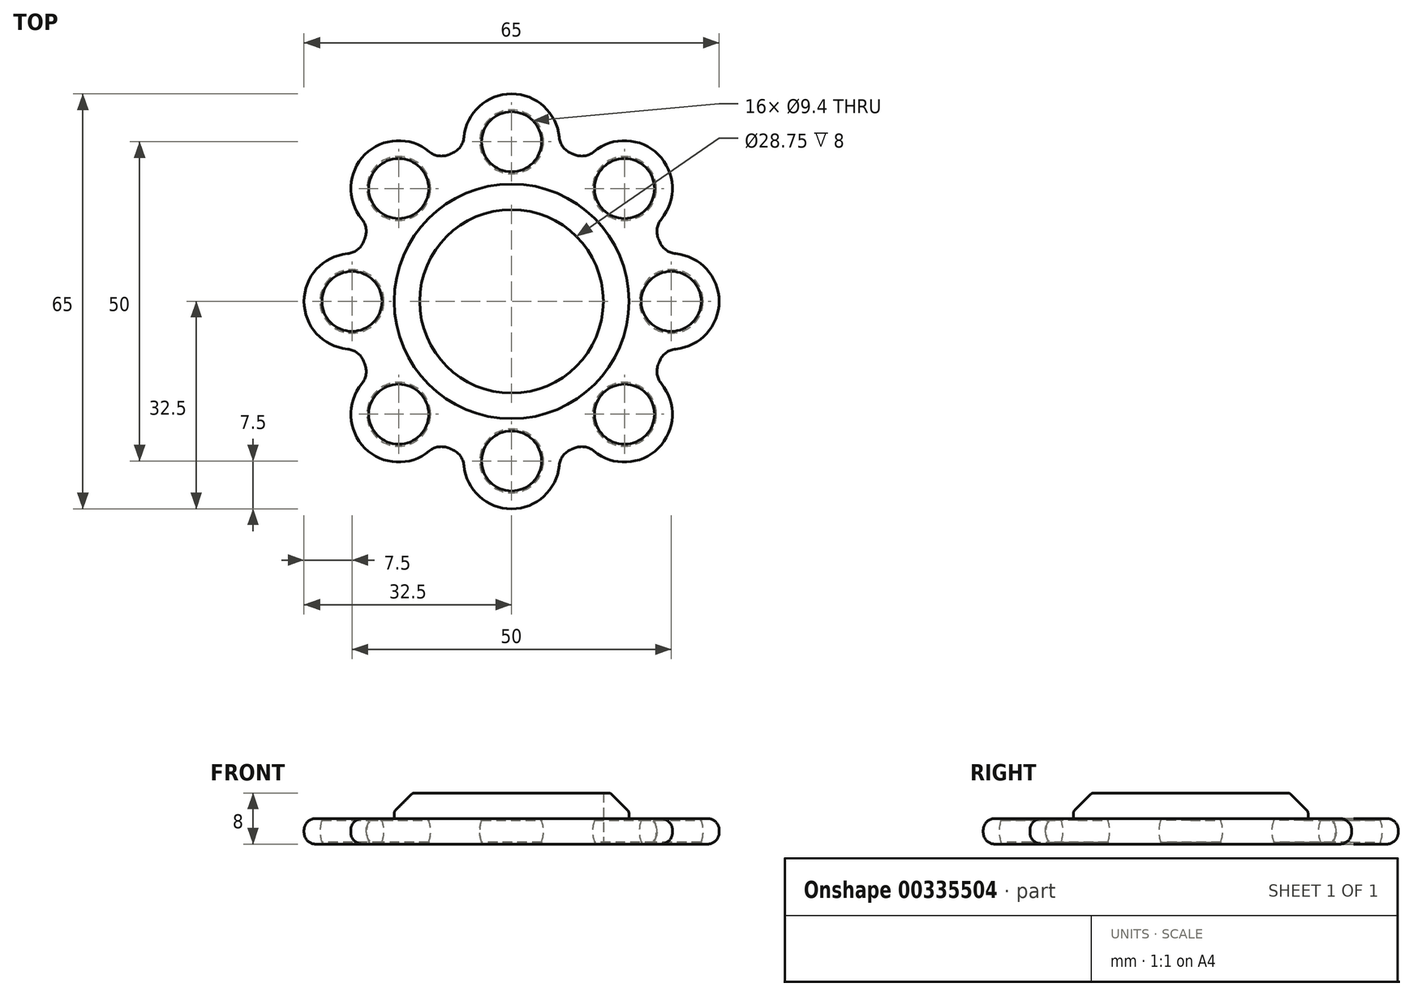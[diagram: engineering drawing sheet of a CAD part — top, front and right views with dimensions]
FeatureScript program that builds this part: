
annotation { "Feature Type Name" : "Feature", "Feature Type Description" : "" }
export const myFeature = defineFeature(function(context is Context, id is Id, definition is map)
    precondition{}
    {
        {
            var Q0;
            Q0=qCreatedBy(makeId("Top.planeOp"),FACE);
            var sketch = newSketch(context, id + "F0", { "sketchPlane" : qUnion([Q0])});
            skCircle(sketch, "E0", {"center": v(0, 0) * mm, "radius": 14.38 * mm});
            skPoint(sketch, "E1.0.midPoint", {"position": v(12.23, 6.82) * mm});
            skCircle(sketch, "E2", {"center": v(0, 25) * mm, "radius": 4.7 * mm});
            skCircle(sketch, "E3.1.0", {"center": v(-17.68, 17.68) * mm, "radius": 4.7 * mm});
            skCircle(sketch, "E3.2.0", {"center": v(-25, 0) * mm, "radius": 4.7 * mm});
            skCircle(sketch, "E3.3.0", {"center": v(-17.68, -17.68) * mm, "radius": 4.7 * mm});
            skCircle(sketch, "E3.4.0", {"center": v(0, -25) * mm, "radius": 4.7 * mm});
            skCircle(sketch, "E3.5.0", {"center": v(17.68, -17.68) * mm, "radius": 4.7 * mm});
            skCircle(sketch, "E3.6.0", {"center": v(25, 0) * mm, "radius": 4.7 * mm});
            skCircle(sketch, "E3.7.0", {"center": v(17.68, 17.68) * mm, "radius": 4.7 * mm});
            skCircle(sketch, "E4", {"center": v(0, 25) * mm, "radius": 7.5 * mm});
            skCircle(sketch, "E5.1.0", {"center": v(-17.68, 17.68) * mm, "radius": 7.5 * mm});
            skCircle(sketch, "E5.2.0", {"center": v(-25, 0) * mm, "radius": 7.5 * mm});
            skCircle(sketch, "E5.3.0", {"center": v(-17.68, -17.68) * mm, "radius": 7.5 * mm});
            skCircle(sketch, "E5.4.0", {"center": v(0, -25) * mm, "radius": 7.5 * mm});
            skCircle(sketch, "E5.5.0", {"center": v(17.68, -17.68) * mm, "radius": 7.5 * mm});
            skCircle(sketch, "E5.6.0", {"center": v(25, 0) * mm, "radius": 7.5 * mm});
            skCircle(sketch, "E5.7.0", {"center": v(17.68, 17.68) * mm, "radius": 7.5 * mm});
            skCircle(sketch, "E6", {"center": v(0, 0) * mm, "radius": 25 * mm});
            skSolve(sketch);
        }
        {
            var Q0;
            Q0=makeQuery(id+"F0.imprint","IMPRINT",FACE,{"disambiguationData":[TD([[makeQuery(id+"F0.imprint","IMPRINT",EDGE,{"derivedFrom":sQuery(id+"F0.wireOp",EDGE,"E0")}),-1.0]])]});
            var Q1;
            {var subQ0=sQuery(id+"F0.wireOp",EDGE,"E6");var subQ1=sQuery(id+"F0.wireOp",EDGE,"E3.3.0");var subQ2=makeQuery(id+"F0.imprint","INTERSECT",VERTEX,{"disambiguationData":[OD(0.0)],"derivedFrom":[subQ1,subQ0]});Q1=makeQuery(id+"F0.imprint","IMPRINT",FACE,{"disambiguationData":[TD([[makeQuery(id+"F0.imprint","IMPRINT",EDGE,{"disambiguationData":[TD([[subQ2,-1.0]])],"derivedFrom":subQ1}),-1.0]])]});}
            var Q2;
            {var subQ0=sQuery(id+"F0.wireOp",EDGE,"E6");var subQ1=sQuery(id+"F0.wireOp",EDGE,"E3.3.0");var subQ2=makeQuery(id+"F0.imprint","INTERSECT",VERTEX,{"disambiguationData":[OD(0.0)],"derivedFrom":[subQ1,subQ0]});Q2=makeQuery(id+"F0.imprint","IMPRINT",FACE,{"disambiguationData":[TD([[makeQuery(id+"F0.imprint","IMPRINT",EDGE,{"disambiguationData":[TD([[subQ2,1.0]])],"derivedFrom":subQ1}),-1.0]])]});}
            var Q3;
            {var subQ0=sQuery(id+"F0.wireOp",EDGE,"E6");var subQ1=sQuery(id+"F0.wireOp",EDGE,"E3.2.0");var subQ2=makeQuery(id+"F0.imprint","INTERSECT",VERTEX,{"disambiguationData":[OD(0.0)],"derivedFrom":[subQ1,subQ0]});Q3=makeQuery(id+"F0.imprint","IMPRINT",FACE,{"disambiguationData":[TD([[makeQuery(id+"F0.imprint","IMPRINT",EDGE,{"disambiguationData":[TD([[subQ2,1.0]])],"derivedFrom":subQ1}),-1.0]])]});}
            var Q4;
            {var subQ0=sQuery(id+"F0.wireOp",EDGE,"E6");var subQ1=sQuery(id+"F0.wireOp",EDGE,"E3.2.0");var subQ2=makeQuery(id+"F0.imprint","INTERSECT",VERTEX,{"disambiguationData":[OD(0.0)],"derivedFrom":[subQ1,subQ0]});Q4=makeQuery(id+"F0.imprint","IMPRINT",FACE,{"disambiguationData":[TD([[makeQuery(id+"F0.imprint","IMPRINT",EDGE,{"disambiguationData":[TD([[subQ2,-1.0]])],"derivedFrom":subQ1}),-1.0]])]});}
            var Q5;
            {var subQ0=sQuery(id+"F0.wireOp",EDGE,"E6");var subQ1=sQuery(id+"F0.wireOp",EDGE,"E3.1.0");var subQ2=makeQuery(id+"F0.imprint","INTERSECT",VERTEX,{"disambiguationData":[OD(0.0)],"derivedFrom":[subQ1,subQ0]});Q5=makeQuery(id+"F0.imprint","IMPRINT",FACE,{"disambiguationData":[TD([[makeQuery(id+"F0.imprint","IMPRINT",EDGE,{"disambiguationData":[TD([[subQ2,-1.0]])],"derivedFrom":subQ1}),-1.0]])]});}
            var Q6;
            {var subQ0=sQuery(id+"F0.wireOp",EDGE,"E6");var subQ1=sQuery(id+"F0.wireOp",EDGE,"E3.1.0");var subQ2=makeQuery(id+"F0.imprint","INTERSECT",VERTEX,{"disambiguationData":[OD(0.0)],"derivedFrom":[subQ1,subQ0]});Q6=makeQuery(id+"F0.imprint","IMPRINT",FACE,{"disambiguationData":[TD([[makeQuery(id+"F0.imprint","IMPRINT",EDGE,{"disambiguationData":[TD([[subQ2,1.0]])],"derivedFrom":subQ1}),-1.0]])]});}
            var Q7;
            {var subQ0=sQuery(id+"F0.wireOp",EDGE,"E6");var subQ1=sQuery(id+"F0.wireOp",EDGE,"E2");var subQ2=makeQuery(id+"F0.imprint","INTERSECT",VERTEX,{"disambiguationData":[OD(0.0)],"derivedFrom":[subQ1,subQ0]});Q7=makeQuery(id+"F0.imprint","IMPRINT",FACE,{"disambiguationData":[TD([[makeQuery(id+"F0.imprint","IMPRINT",EDGE,{"disambiguationData":[TD([[subQ2,1.0]])],"derivedFrom":subQ1}),-1.0]])]});}
            var Q8;
            {var subQ0=sQuery(id+"F0.wireOp",EDGE,"E6");var subQ1=sQuery(id+"F0.wireOp",EDGE,"E2");var subQ2=makeQuery(id+"F0.imprint","INTERSECT",VERTEX,{"disambiguationData":[OD(0.0)],"derivedFrom":[subQ1,subQ0]});Q8=makeQuery(id+"F0.imprint","IMPRINT",FACE,{"disambiguationData":[TD([[makeQuery(id+"F0.imprint","IMPRINT",EDGE,{"disambiguationData":[TD([[subQ2,-1.0]])],"derivedFrom":subQ1}),-1.0]])]});}
            var Q9;
            {var subQ0=sQuery(id+"F0.wireOp",EDGE,"E6");var subQ1=sQuery(id+"F0.wireOp",EDGE,"E3.7.0");var subQ2=makeQuery(id+"F0.imprint","INTERSECT",VERTEX,{"disambiguationData":[OD(0.0)],"derivedFrom":[subQ1,subQ0]});Q9=makeQuery(id+"F0.imprint","IMPRINT",FACE,{"disambiguationData":[TD([[makeQuery(id+"F0.imprint","IMPRINT",EDGE,{"disambiguationData":[TD([[subQ2,1.0]])],"derivedFrom":subQ1}),-1.0]])]});}
            var Q10;
            {var subQ0=sQuery(id+"F0.wireOp",EDGE,"E6");var subQ1=sQuery(id+"F0.wireOp",EDGE,"E3.7.0");var subQ2=makeQuery(id+"F0.imprint","INTERSECT",VERTEX,{"disambiguationData":[OD(0.0)],"derivedFrom":[subQ1,subQ0]});Q10=makeQuery(id+"F0.imprint","IMPRINT",FACE,{"disambiguationData":[TD([[makeQuery(id+"F0.imprint","IMPRINT",EDGE,{"disambiguationData":[TD([[subQ2,-1.0]])],"derivedFrom":subQ1}),-1.0]])]});}
            var Q11;
            {var subQ0=sQuery(id+"F0.wireOp",EDGE,"E6");var subQ1=sQuery(id+"F0.wireOp",EDGE,"E3.6.0");var subQ2=makeQuery(id+"F0.imprint","INTERSECT",VERTEX,{"disambiguationData":[OD(0.0)],"derivedFrom":[subQ1,subQ0]});Q11=makeQuery(id+"F0.imprint","IMPRINT",FACE,{"disambiguationData":[TD([[makeQuery(id+"F0.imprint","IMPRINT",EDGE,{"disambiguationData":[TD([[subQ2,-1.0]])],"derivedFrom":subQ1}),-1.0]])]});}
            var Q12;
            {var subQ0=sQuery(id+"F0.wireOp",EDGE,"E6");var subQ1=sQuery(id+"F0.wireOp",EDGE,"E3.6.0");var subQ2=makeQuery(id+"F0.imprint","INTERSECT",VERTEX,{"disambiguationData":[OD(0.0)],"derivedFrom":[subQ1,subQ0]});Q12=makeQuery(id+"F0.imprint","IMPRINT",FACE,{"disambiguationData":[TD([[makeQuery(id+"F0.imprint","IMPRINT",EDGE,{"disambiguationData":[TD([[subQ2,1.0]])],"derivedFrom":subQ1}),-1.0]])]});}
            var Q13;
            {var subQ0=sQuery(id+"F0.wireOp",EDGE,"E6");var subQ1=sQuery(id+"F0.wireOp",EDGE,"E3.5.0");var subQ2=makeQuery(id+"F0.imprint","INTERSECT",VERTEX,{"disambiguationData":[OD(0.0)],"derivedFrom":[subQ1,subQ0]});Q13=makeQuery(id+"F0.imprint","IMPRINT",FACE,{"disambiguationData":[TD([[makeQuery(id+"F0.imprint","IMPRINT",EDGE,{"disambiguationData":[TD([[subQ2,1.0]])],"derivedFrom":subQ1}),-1.0]])]});}
            var Q14;
            {var subQ0=sQuery(id+"F0.wireOp",EDGE,"E6");var subQ1=sQuery(id+"F0.wireOp",EDGE,"E3.5.0");var subQ2=makeQuery(id+"F0.imprint","INTERSECT",VERTEX,{"disambiguationData":[OD(0.0)],"derivedFrom":[subQ1,subQ0]});Q14=makeQuery(id+"F0.imprint","IMPRINT",FACE,{"disambiguationData":[TD([[makeQuery(id+"F0.imprint","IMPRINT",EDGE,{"disambiguationData":[TD([[subQ2,-1.0]])],"derivedFrom":subQ1}),-1.0]])]});}
            var Q15;
            {var subQ0=sQuery(id+"F0.wireOp",EDGE,"E6");var subQ1=sQuery(id+"F0.wireOp",EDGE,"E3.4.0");var subQ2=makeQuery(id+"F0.imprint","INTERSECT",VERTEX,{"disambiguationData":[OD(0.0)],"derivedFrom":[subQ1,subQ0]});Q15=makeQuery(id+"F0.imprint","IMPRINT",FACE,{"disambiguationData":[TD([[makeQuery(id+"F0.imprint","IMPRINT",EDGE,{"disambiguationData":[TD([[subQ2,1.0]])],"derivedFrom":subQ1}),-1.0]])]});}
            var Q16;
            {var subQ0=sQuery(id+"F0.wireOp",EDGE,"E6");var subQ1=sQuery(id+"F0.wireOp",EDGE,"E3.4.0");var subQ2=makeQuery(id+"F0.imprint","INTERSECT",VERTEX,{"disambiguationData":[OD(0.0)],"derivedFrom":[subQ1,subQ0]});Q16=makeQuery(id+"F0.imprint","IMPRINT",FACE,{"disambiguationData":[TD([[makeQuery(id+"F0.imprint","IMPRINT",EDGE,{"disambiguationData":[TD([[subQ2,-1.0]])],"derivedFrom":subQ1}),-1.0]])]});}
            extrude(context, id + "F1", {"entities" : qUnion([Q0, Q1, Q2, Q3, Q4, Q5, Q6, Q7, Q8, Q9, Q10, Q11, Q12, Q13, Q14, Q15, Q16]), "depth" : 2 * mm, "hasSecondDirection" : true, "secondDirectionOppositeDirection" : true, "secondDirectionDepth" : 2 * mm});
        }
        {
            var Q0;
            {var subQ0=sQuery(id+"F0.wireOp",EDGE,"E6");var subQ1=sQuery(id+"F0.wireOp",EDGE,"E5.4.0");Q0=makeQuery(id+"F1.opExtrude","SWEPT_EDGE",EDGE,{"disambiguationData":[OSD([subQ1,subQ0]),TDD([makeQuery(id+"F0.imprint","INTERSECT",VERTEX,{"disambiguationData":[OD(0.0)],"derivedFrom":[subQ1,subQ0]})])]});}
            var Q1;
            {var subQ0=sQuery(id+"F0.wireOp",EDGE,"E6");var subQ1=sQuery(id+"F0.wireOp",EDGE,"E5.2.0");Q1=makeQuery(id+"F1.opExtrude","SWEPT_EDGE",EDGE,{"disambiguationData":[OSD([subQ1,subQ0]),TDD([makeQuery(id+"F0.imprint","INTERSECT",VERTEX,{"disambiguationData":[OD(1.0)],"derivedFrom":[subQ1,subQ0]})])]});}
            var Q2;
            {var subQ0=sQuery(id+"F0.wireOp",EDGE,"E6");var subQ1=sQuery(id+"F0.wireOp",EDGE,"E5.2.0");Q2=makeQuery(id+"F1.opExtrude","SWEPT_EDGE",EDGE,{"disambiguationData":[OSD([subQ1,subQ0]),TDD([makeQuery(id+"F0.imprint","INTERSECT",VERTEX,{"disambiguationData":[OD(0.0)],"derivedFrom":[subQ1,subQ0]})])]});}
            var Q3;
            {var subQ0=sQuery(id+"F0.wireOp",EDGE,"E6");var subQ1=sQuery(id+"F0.wireOp",EDGE,"E4");Q3=makeQuery(id+"F1.opExtrude","SWEPT_EDGE",EDGE,{"disambiguationData":[OSD([subQ1,subQ0]),TDD([makeQuery(id+"F0.imprint","INTERSECT",VERTEX,{"disambiguationData":[OD(1.0)],"derivedFrom":[subQ1,subQ0]})])]});}
            var Q4;
            {var subQ0=sQuery(id+"F0.wireOp",EDGE,"E6");var subQ1=sQuery(id+"F0.wireOp",EDGE,"E5.7.0");Q4=makeQuery(id+"F1.opExtrude","SWEPT_EDGE",EDGE,{"disambiguationData":[OSD([subQ1,subQ0]),TDD([makeQuery(id+"F0.imprint","INTERSECT",VERTEX,{"disambiguationData":[OD(1.0)],"derivedFrom":[subQ1,subQ0]})])]});}
            var Q5;
            {var subQ0=sQuery(id+"F0.wireOp",EDGE,"E6");var subQ1=sQuery(id+"F0.wireOp",EDGE,"E5.1.0");Q5=makeQuery(id+"F1.opExtrude","SWEPT_EDGE",EDGE,{"disambiguationData":[OSD([subQ1,subQ0]),TDD([makeQuery(id+"F0.imprint","INTERSECT",VERTEX,{"disambiguationData":[OD(1.0)],"derivedFrom":[subQ1,subQ0]})])]});}
            var Q6;
            {var subQ0=sQuery(id+"F0.wireOp",EDGE,"E6");var subQ1=sQuery(id+"F0.wireOp",EDGE,"E5.3.0");Q6=makeQuery(id+"F1.opExtrude","SWEPT_EDGE",EDGE,{"disambiguationData":[OSD([subQ1,subQ0]),TDD([makeQuery(id+"F0.imprint","INTERSECT",VERTEX,{"disambiguationData":[OD(0.0)],"derivedFrom":[subQ1,subQ0]})])]});}
            var Q7;
            {var subQ0=sQuery(id+"F0.wireOp",EDGE,"E6");var subQ1=sQuery(id+"F0.wireOp",EDGE,"E5.1.0");Q7=makeQuery(id+"F1.opExtrude","SWEPT_EDGE",EDGE,{"disambiguationData":[OSD([subQ1,subQ0]),TDD([makeQuery(id+"F0.imprint","INTERSECT",VERTEX,{"disambiguationData":[OD(0.0)],"derivedFrom":[subQ1,subQ0]})])]});}
            var Q8;
            {var subQ0=sQuery(id+"F0.wireOp",EDGE,"E6");var subQ1=sQuery(id+"F0.wireOp",EDGE,"E4");Q8=makeQuery(id+"F1.opExtrude","SWEPT_EDGE",EDGE,{"disambiguationData":[OSD([subQ1,subQ0]),TDD([makeQuery(id+"F0.imprint","INTERSECT",VERTEX,{"disambiguationData":[OD(0.0)],"derivedFrom":[subQ1,subQ0]})])]});}
            var Q9;
            {var subQ0=sQuery(id+"F0.wireOp",EDGE,"E6");var subQ1=sQuery(id+"F0.wireOp",EDGE,"E5.6.0");Q9=makeQuery(id+"F1.opExtrude","SWEPT_EDGE",EDGE,{"disambiguationData":[OSD([subQ1,subQ0]),TDD([makeQuery(id+"F0.imprint","INTERSECT",VERTEX,{"disambiguationData":[OD(0.0)],"derivedFrom":[subQ1,subQ0]})])]});}
            var Q10;
            {var subQ0=sQuery(id+"F0.wireOp",EDGE,"E6");var subQ1=sQuery(id+"F0.wireOp",EDGE,"E5.7.0");Q10=makeQuery(id+"F1.opExtrude","SWEPT_EDGE",EDGE,{"disambiguationData":[OSD([subQ1,subQ0]),TDD([makeQuery(id+"F0.imprint","INTERSECT",VERTEX,{"disambiguationData":[OD(0.0)],"derivedFrom":[subQ1,subQ0]})])]});}
            var Q11;
            {var subQ0=sQuery(id+"F0.wireOp",EDGE,"E6");var subQ1=sQuery(id+"F0.wireOp",EDGE,"E5.6.0");Q11=makeQuery(id+"F1.opExtrude","SWEPT_EDGE",EDGE,{"disambiguationData":[OSD([subQ1,subQ0]),TDD([makeQuery(id+"F0.imprint","INTERSECT",VERTEX,{"disambiguationData":[OD(1.0)],"derivedFrom":[subQ1,subQ0]})])]});}
            var Q12;
            {var subQ0=sQuery(id+"F0.wireOp",EDGE,"E6");var subQ1=sQuery(id+"F0.wireOp",EDGE,"E5.5.0");Q12=makeQuery(id+"F1.opExtrude","SWEPT_EDGE",EDGE,{"disambiguationData":[OSD([subQ1,subQ0]),TDD([makeQuery(id+"F0.imprint","INTERSECT",VERTEX,{"disambiguationData":[OD(1.0)],"derivedFrom":[subQ1,subQ0]})])]});}
            var Q13;
            {var subQ0=sQuery(id+"F0.wireOp",EDGE,"E6");var subQ1=sQuery(id+"F0.wireOp",EDGE,"E5.5.0");Q13=makeQuery(id+"F1.opExtrude","SWEPT_EDGE",EDGE,{"disambiguationData":[OSD([subQ1,subQ0]),TDD([makeQuery(id+"F0.imprint","INTERSECT",VERTEX,{"disambiguationData":[OD(0.0)],"derivedFrom":[subQ1,subQ0]})])]});}
            var Q14;
            {var subQ0=sQuery(id+"F0.wireOp",EDGE,"E6");var subQ1=sQuery(id+"F0.wireOp",EDGE,"E5.4.0");Q14=makeQuery(id+"F1.opExtrude","SWEPT_EDGE",EDGE,{"disambiguationData":[OSD([subQ1,subQ0]),TDD([makeQuery(id+"F0.imprint","INTERSECT",VERTEX,{"disambiguationData":[OD(1.0)],"derivedFrom":[subQ1,subQ0]})])]});}
            var Q15;
            {var subQ0=sQuery(id+"F0.wireOp",EDGE,"E6");var subQ1=sQuery(id+"F0.wireOp",EDGE,"E5.3.0");Q15=makeQuery(id+"F1.opExtrude","SWEPT_EDGE",EDGE,{"disambiguationData":[OSD([subQ1,subQ0]),TDD([makeQuery(id+"F0.imprint","INTERSECT",VERTEX,{"disambiguationData":[OD(1.0)],"derivedFrom":[subQ1,subQ0]})])]});}
            fillet(context, id + "F2", {"entities" : qUnion([Q0, Q1, Q2, Q3, Q4, Q5, Q6, Q7, Q8, Q9, Q10, Q11, Q12, Q13, Q14, Q15]), "radius" : 3 * mm, "tangentPropagation" : true, "allowEdgeOverflow" : false});
        }
        {
            var Q0;
            Q0=makeQuery(id+"F1.opExtrude","CAP_EDGE",EDGE,{"disambiguationData":[OSD([sQuery(id+"F0.wireOp",EDGE,"E5.7.0")])],"isStart":false});
            var Q1;
            Q1=makeQuery(id+"F1.opExtrude","CAP_EDGE",EDGE,{"disambiguationData":[OSD([sQuery(id+"F0.wireOp",EDGE,"E5.7.0")])],"isStart":true});
            fillet(context, id + "F3", {"entities" : qUnion([Q0, Q1]), "radius" : 1.8 * mm, "tangentPropagation" : true, "allowEdgeOverflow" : false});
        }
        {
            var Q0;
            Q0=qCreatedBy(makeId("Right.planeOp"),FACE);
            var sketch = newSketch(context, id + "F4", { "sketchPlane" : qUnion([Q0])});
            skPoint(sketch, "E7.0", {"position": v(-25, 0) * mm});
            skPoint(sketch, "E7.1", {"position": v(25, 0) * mm});
            skLineSegment(sketch, "E8", {"start": v(-25, 12.35) * mm, "end": v(-25, -14.21) * mm, "construction": true});
            skLineSegment(sketch, "E9", {"start": v(25, 12.16) * mm, "end": v(25, -14.21) * mm, "construction": true});
            skPoint(sketch, "E10", {"position": v(-25, 5) * mm});
            skPoint(sketch, "E11", {"position": v(-25, -5) * mm});
            skPoint(sketch, "E12", {"position": v(25, 5) * mm});
            skPoint(sketch, "E13", {"position": v(25, -5) * mm});
            skArc(sketch, "E14", {"start": v(-25, 5) * mm, "mid": v(-30, 0) * mm, "end": v(-25, -5) * mm});
            skArc(sketch, "E15", {"start": v(25, -5) * mm, "mid": v(30, 0) * mm, "end": v(25, 5) * mm});
            skLineSegment(sketch, "E16", {"start": v(-25, 5) * mm, "end": v(-25, -5) * mm});
            skLineSegment(sketch, "E17", {"start": v(25, 5) * mm, "end": v(25, -5) * mm});
            skLineSegment(sketch, "E18", {"start": v(0, 41.23) * mm, "end": v(0, -49.38) * mm, "construction": true});
            skSolve(sketch);
        }
        {
            var Q0;
            Q0=makeQuery(id+"F4.imprint","IMPRINT",FACE,{"disambiguationData":[TD([[makeQuery(id+"F4.imprint","IMPRINT",EDGE,{"derivedFrom":sQuery(id+"F4.wireOp",EDGE,"E14")}),1.0]])]});
            var Q1;
            Q1=sQuery(id+"F4.wireOp",EDGE,"E8");
            revolve(context, id + "F5", {"entities" : qUnion([Q0]), "axis" : qUnion([Q1]), "revolveType" : RevolveType.FULL});
        }
        {
            var Q0;
            Q0=makeQuery(id+"F4.imprint","IMPRINT",FACE,{"disambiguationData":[TD([[makeQuery(id+"F4.imprint","IMPRINT",EDGE,{"derivedFrom":sQuery(id+"F4.wireOp",EDGE,"E15")}),1.0]])]});
            var Q1;
            Q1=sQuery(id+"F4.wireOp",EDGE,"E9");
            revolve(context, id + "F6", {"entities" : qUnion([Q0]), "axis" : qUnion([Q1]), "revolveType" : RevolveType.FULL});
        }
        {
            var Q0;
            Q0=makeQuery(id+"F6.opRevolve","SWEPT_BODY",BODY,{"disambiguationData":[OSD([sQuery(id+"F4.wireOp",EDGE,"E15"),sQuery(id+"F4.wireOp",EDGE,"E17")])]});
            var Q1;
            Q1=makeQuery(id+"F5.opRevolve","SWEPT_BODY",BODY,{"disambiguationData":[OSD([sQuery(id+"F4.wireOp",EDGE,"E14"),sQuery(id+"F4.wireOp",EDGE,"E16")])]});
            var Q2;
            Q2=makeQuery(id+"F1.opExtrude","SWEPT_BODY",BODY,{"disambiguationData":[OSD([sQuery(id+"F0.wireOp",EDGE,"E0"),sQuery(id+"F0.wireOp",EDGE,"E2"),sQuery(id+"F0.wireOp",EDGE,"E3.1.0"),sQuery(id+"F0.wireOp",EDGE,"E3.2.0"),sQuery(id+"F0.wireOp",EDGE,"E3.3.0"),sQuery(id+"F0.wireOp",EDGE,"E3.4.0"),sQuery(id+"F0.wireOp",EDGE,"E3.5.0"),sQuery(id+"F0.wireOp",EDGE,"E3.6.0"),sQuery(id+"F0.wireOp",EDGE,"E3.7.0"),sQuery(id+"F0.wireOp",EDGE,"E4"),sQuery(id+"F0.wireOp",EDGE,"E5.1.0"),sQuery(id+"F0.wireOp",EDGE,"E5.2.0"),sQuery(id+"F0.wireOp",EDGE,"E5.3.0"),sQuery(id+"F0.wireOp",EDGE,"E5.4.0"),sQuery(id+"F0.wireOp",EDGE,"E5.5.0"),sQuery(id+"F0.wireOp",EDGE,"E5.6.0"),sQuery(id+"F0.wireOp",EDGE,"E5.7.0"),sQuery(id+"F0.wireOp",EDGE,"E6")])]});
            booleanBodies(context, id + "F7", {"operationType" : BooleanOperationType.SUBTRACTION, "tools" : qUnion([Q0, Q1]), "targets" : qUnion([Q2])});
        }
        {
            var Q0;
            Q0=qCreatedBy(makeId("Front.planeOp"),FACE);
            var sketch = newSketch(context, id + "F8", { "sketchPlane" : qUnion([Q0])});
            skPoint(sketch, "E19.0", {"position": v(-25, 0) * mm});
            skPoint(sketch, "E19.1", {"position": v(25, 0) * mm});
            skLineSegment(sketch, "E20", {"start": v(-25, 18.9) * mm, "end": v(-25, -20.91) * mm, "construction": true});
            skLineSegment(sketch, "E21", {"start": v(25, 20.02) * mm, "end": v(25, -22.02) * mm, "construction": true});
            skPoint(sketch, "E22", {"position": v(-25, 5) * mm});
            skPoint(sketch, "E23", {"position": v(-25, -5) * mm});
            skPoint(sketch, "E24", {"position": v(25, 5) * mm});
            skPoint(sketch, "E25", {"position": v(25, -5) * mm});
            skArc(sketch, "E26", {"start": v(-25, 5) * mm, "mid": v(-30, 0) * mm, "end": v(-25, -5) * mm});
            skArc(sketch, "E27", {"start": v(25, -5) * mm, "mid": v(30, 0) * mm, "end": v(25, 5) * mm});
            skLineSegment(sketch, "E28", {"start": v(-25, 5) * mm, "end": v(-25, -5) * mm});
            skLineSegment(sketch, "E29", {"start": v(25, 5) * mm, "end": v(25, -5) * mm});
            skSolve(sketch);
        }
        {
            var Q0;
            Q0=makeQuery(id+"F8.imprint","IMPRINT",FACE,{"disambiguationData":[TD([[makeQuery(id+"F8.imprint","IMPRINT",EDGE,{"derivedFrom":sQuery(id+"F8.wireOp",EDGE,"E26")}),1.0]])]});
            var Q1;
            Q1=sQuery(id+"F8.wireOp",EDGE,"E20");
            revolve(context, id + "F9", {"entities" : qUnion([Q0]), "axis" : qUnion([Q1]), "revolveType" : RevolveType.FULL});
        }
        {
            var Q0;
            Q0=makeQuery(id+"F8.imprint","IMPRINT",FACE,{"disambiguationData":[TD([[makeQuery(id+"F8.imprint","IMPRINT",EDGE,{"derivedFrom":sQuery(id+"F8.wireOp",EDGE,"E27")}),1.0]])]});
            var Q1;
            Q1=sQuery(id+"F8.wireOp",EDGE,"E21");
            revolve(context, id + "F10", {"entities" : qUnion([Q0]), "axis" : qUnion([Q1]), "revolveType" : RevolveType.FULL});
        }
        {
            var Q0;
            Q0=makeQuery(id+"F9.opRevolve","SWEPT_BODY",BODY,{"disambiguationData":[OSD([sQuery(id+"F8.wireOp",EDGE,"E26"),sQuery(id+"F8.wireOp",EDGE,"E28")])]});
            var Q1;
            Q1=makeQuery(id+"F10.opRevolve","SWEPT_BODY",BODY,{"disambiguationData":[OSD([sQuery(id+"F8.wireOp",EDGE,"E27"),sQuery(id+"F8.wireOp",EDGE,"E29")])]});
            var Q2;
            Q2=makeQuery(id+"F1.opExtrude","SWEPT_BODY",BODY,{"disambiguationData":[OSD([sQuery(id+"F0.wireOp",EDGE,"E0"),sQuery(id+"F0.wireOp",EDGE,"E2"),sQuery(id+"F0.wireOp",EDGE,"E3.1.0"),sQuery(id+"F0.wireOp",EDGE,"E3.2.0"),sQuery(id+"F0.wireOp",EDGE,"E3.3.0"),sQuery(id+"F0.wireOp",EDGE,"E3.4.0"),sQuery(id+"F0.wireOp",EDGE,"E3.5.0"),sQuery(id+"F0.wireOp",EDGE,"E3.6.0"),sQuery(id+"F0.wireOp",EDGE,"E3.7.0"),sQuery(id+"F0.wireOp",EDGE,"E4"),sQuery(id+"F0.wireOp",EDGE,"E5.1.0"),sQuery(id+"F0.wireOp",EDGE,"E5.2.0"),sQuery(id+"F0.wireOp",EDGE,"E5.3.0"),sQuery(id+"F0.wireOp",EDGE,"E5.4.0"),sQuery(id+"F0.wireOp",EDGE,"E5.5.0"),sQuery(id+"F0.wireOp",EDGE,"E5.6.0"),sQuery(id+"F0.wireOp",EDGE,"E5.7.0"),sQuery(id+"F0.wireOp",EDGE,"E6")])]});
            booleanBodies(context, id + "F11", {"operationType" : BooleanOperationType.SUBTRACTION, "tools" : qUnion([Q0, Q1]), "targets" : qUnion([Q2])});
        }
        {
            var Q0;
            Q0=qCreatedBy(makeId("Front.planeOp"),FACE);
            var Q1;
            Q1=sQuery(id+"F0.wireOp",VERTEX,"E3.3.0.center");
            cPlane(context, id + "F12", {"entities" : qUnion([Q0, Q1]), "cplaneType" : CPlaneType.PLANE_POINT, "offset" : 25 * mm, "width" : 150 * mm, "height" : 150 * mm});
        }
        {
            var Q0;
            Q0=qCreatedBy(id+"F12.planeOp",FACE);
            var sketch = newSketch(context, id + "F13", { "sketchPlane" : qUnion([Q0])});
            skPoint(sketch, "E30.0", {"position": v(-17.68, 0) * mm});
            skPoint(sketch, "E30.1", {"position": v(17.68, 0) * mm});
            skLineSegment(sketch, "E31", {"start": v(-17.68, 20.76) * mm, "end": v(-17.68, -25.8) * mm, "construction": true});
            skLineSegment(sketch, "E32", {"start": v(17.68, 18.25) * mm, "end": v(17.68, -22.97) * mm, "construction": true});
            skPoint(sketch, "E33", {"position": v(-17.68, 5) * mm});
            skPoint(sketch, "E34", {"position": v(-17.68, -5) * mm});
            skPoint(sketch, "E35", {"position": v(17.68, -5) * mm});
            skPoint(sketch, "E36", {"position": v(17.68, 5) * mm});
            skArc(sketch, "E37", {"start": v(-17.68, 5) * mm, "mid": v(-22.68, 0) * mm, "end": v(-17.68, -5) * mm});
            skArc(sketch, "E38", {"start": v(17.68, -5) * mm, "mid": v(22.68, 0) * mm, "end": v(17.68, 5) * mm});
            skLineSegment(sketch, "E39", {"start": v(-17.68, 5) * mm, "end": v(-17.68, -5) * mm});
            skLineSegment(sketch, "E40", {"start": v(17.68, 5) * mm, "end": v(17.68, -5) * mm});
            skSolve(sketch);
        }
        {
            var Q0;
            Q0=makeQuery(id+"F13.imprint","IMPRINT",FACE,{"disambiguationData":[TD([[makeQuery(id+"F13.imprint","IMPRINT",EDGE,{"derivedFrom":sQuery(id+"F13.wireOp",EDGE,"E37")}),1.0]])]});
            var Q1;
            Q1=sQuery(id+"F13.wireOp",EDGE,"E31");
            revolve(context, id + "F14", {"entities" : qUnion([Q0]), "axis" : qUnion([Q1]), "revolveType" : RevolveType.FULL});
        }
        {
            var Q0;
            Q0=makeQuery(id+"F13.imprint","IMPRINT",FACE,{"disambiguationData":[TD([[makeQuery(id+"F13.imprint","IMPRINT",EDGE,{"derivedFrom":sQuery(id+"F13.wireOp",EDGE,"E38")}),1.0]])]});
            var Q1;
            Q1=sQuery(id+"F13.wireOp",EDGE,"E32");
            revolve(context, id + "F15", {"entities" : qUnion([Q0]), "axis" : qUnion([Q1]), "revolveType" : RevolveType.FULL});
        }
        {
            var Q0;
            Q0=makeQuery(id+"F15.opRevolve","SWEPT_BODY",BODY,{"disambiguationData":[OSD([sQuery(id+"F13.wireOp",EDGE,"E38"),sQuery(id+"F13.wireOp",EDGE,"E40")])]});
            var Q1;
            Q1=makeQuery(id+"F14.opRevolve","SWEPT_BODY",BODY,{"disambiguationData":[OSD([sQuery(id+"F13.wireOp",EDGE,"E37"),sQuery(id+"F13.wireOp",EDGE,"E39")])]});
            var Q2;
            Q2=makeQuery(id+"F1.opExtrude","SWEPT_BODY",BODY,{"disambiguationData":[OSD([sQuery(id+"F0.wireOp",EDGE,"E0"),sQuery(id+"F0.wireOp",EDGE,"E2"),sQuery(id+"F0.wireOp",EDGE,"E3.1.0"),sQuery(id+"F0.wireOp",EDGE,"E3.2.0"),sQuery(id+"F0.wireOp",EDGE,"E3.3.0"),sQuery(id+"F0.wireOp",EDGE,"E3.4.0"),sQuery(id+"F0.wireOp",EDGE,"E3.5.0"),sQuery(id+"F0.wireOp",EDGE,"E3.6.0"),sQuery(id+"F0.wireOp",EDGE,"E3.7.0"),sQuery(id+"F0.wireOp",EDGE,"E4"),sQuery(id+"F0.wireOp",EDGE,"E5.1.0"),sQuery(id+"F0.wireOp",EDGE,"E5.2.0"),sQuery(id+"F0.wireOp",EDGE,"E5.3.0"),sQuery(id+"F0.wireOp",EDGE,"E5.4.0"),sQuery(id+"F0.wireOp",EDGE,"E5.5.0"),sQuery(id+"F0.wireOp",EDGE,"E5.6.0"),sQuery(id+"F0.wireOp",EDGE,"E5.7.0"),sQuery(id+"F0.wireOp",EDGE,"E6")])]});
            booleanBodies(context, id + "F16", {"operationType" : BooleanOperationType.SUBTRACTION, "tools" : qUnion([Q0, Q1]), "targets" : qUnion([Q2])});
        }
        {
            var Q0;
            Q0=qCreatedBy(makeId("Front.planeOp"),FACE);
            var Q1;
            Q1=sQuery(id+"F0.wireOp",VERTEX,"E5.7.0.center");
            cPlane(context, id + "F17", {"entities" : qUnion([Q0, Q1]), "cplaneType" : CPlaneType.PLANE_POINT, "offset" : 25 * mm, "width" : 150 * mm, "height" : 150 * mm});
        }
        {
            var Q0;
            Q0=qCreatedBy(id+"F17.planeOp",FACE);
            var sketch = newSketch(context, id + "F18", { "sketchPlane" : qUnion([Q0])});
            skPoint(sketch, "E41.0", {"position": v(17.68, 0) * mm});
            skPoint(sketch, "E41.1", {"position": v(-17.68, 0) * mm});
            skLineSegment(sketch, "E42", {"start": v(17.68, 20.69) * mm, "end": v(17.68, -19.13) * mm, "construction": true});
            skLineSegment(sketch, "E43", {"start": v(-17.68, 22.25) * mm, "end": v(-17.68, -19.13) * mm, "construction": true});
            skPoint(sketch, "E44", {"position": v(17.68, 5) * mm});
            skPoint(sketch, "E45", {"position": v(-17.68, 5) * mm});
            skPoint(sketch, "E46", {"position": v(17.68, -5) * mm});
            skPoint(sketch, "E47", {"position": v(-17.68, -5) * mm});
            skArc(sketch, "E48", {"start": v(17.68, -5) * mm, "mid": v(22.68, 0) * mm, "end": v(17.68, 5) * mm});
            skArc(sketch, "E49", {"start": v(-17.68, 5) * mm, "mid": v(-22.68, 0) * mm, "end": v(-17.68, -5) * mm});
            skLineSegment(sketch, "E50", {"start": v(17.68, 5) * mm, "end": v(17.68, -5) * mm});
            skLineSegment(sketch, "E51", {"start": v(-17.68, 5) * mm, "end": v(-17.68, -5) * mm});
            skSolve(sketch);
        }
        {
            var Q0;
            Q0=makeQuery(id+"F18.imprint","IMPRINT",FACE,{"disambiguationData":[TD([[makeQuery(id+"F18.imprint","IMPRINT",EDGE,{"derivedFrom":sQuery(id+"F18.wireOp",EDGE,"E48")}),1.0]])]});
            var Q1;
            Q1=sQuery(id+"F18.wireOp",EDGE,"E42");
            revolve(context, id + "F19", {"entities" : qUnion([Q0]), "axis" : qUnion([Q1]), "revolveType" : RevolveType.FULL});
        }
        {
            var Q0;
            Q0=makeQuery(id+"F18.imprint","IMPRINT",FACE,{"disambiguationData":[TD([[makeQuery(id+"F18.imprint","IMPRINT",EDGE,{"derivedFrom":sQuery(id+"F18.wireOp",EDGE,"E49")}),1.0]])]});
            var Q1;
            Q1=sQuery(id+"F18.wireOp",EDGE,"E43");
            revolve(context, id + "F20", {"entities" : qUnion([Q0]), "axis" : qUnion([Q1]), "revolveType" : RevolveType.FULL});
        }
        {
            var Q0;
            Q0=makeQuery(id+"F20.opRevolve","SWEPT_BODY",BODY,{"disambiguationData":[OSD([sQuery(id+"F18.wireOp",EDGE,"E49"),sQuery(id+"F18.wireOp",EDGE,"E51")])]});
            var Q1;
            Q1=makeQuery(id+"F19.opRevolve","SWEPT_BODY",BODY,{"disambiguationData":[OSD([sQuery(id+"F18.wireOp",EDGE,"E48"),sQuery(id+"F18.wireOp",EDGE,"E50")])]});
            var Q2;
            Q2=makeQuery(id+"F1.opExtrude","SWEPT_BODY",BODY,{"disambiguationData":[OSD([sQuery(id+"F0.wireOp",EDGE,"E0"),sQuery(id+"F0.wireOp",EDGE,"E2"),sQuery(id+"F0.wireOp",EDGE,"E3.1.0"),sQuery(id+"F0.wireOp",EDGE,"E3.2.0"),sQuery(id+"F0.wireOp",EDGE,"E3.3.0"),sQuery(id+"F0.wireOp",EDGE,"E3.4.0"),sQuery(id+"F0.wireOp",EDGE,"E3.5.0"),sQuery(id+"F0.wireOp",EDGE,"E3.6.0"),sQuery(id+"F0.wireOp",EDGE,"E3.7.0"),sQuery(id+"F0.wireOp",EDGE,"E4"),sQuery(id+"F0.wireOp",EDGE,"E5.1.0"),sQuery(id+"F0.wireOp",EDGE,"E5.2.0"),sQuery(id+"F0.wireOp",EDGE,"E5.3.0"),sQuery(id+"F0.wireOp",EDGE,"E5.4.0"),sQuery(id+"F0.wireOp",EDGE,"E5.5.0"),sQuery(id+"F0.wireOp",EDGE,"E5.6.0"),sQuery(id+"F0.wireOp",EDGE,"E5.7.0"),sQuery(id+"F0.wireOp",EDGE,"E6")])]});
            booleanBodies(context, id + "F21", {"operationType" : BooleanOperationType.SUBTRACTION, "tools" : qUnion([Q0, Q1]), "targets" : qUnion([Q2])});
        }
        {
            var Q0;
            Q0=makeQuery(id+"F1.opExtrude","CAP_FACE",FACE,{"disambiguationData":[OSD([sQuery(id+"F0.wireOp",EDGE,"E0"),sQuery(id+"F0.wireOp",EDGE,"E2"),sQuery(id+"F0.wireOp",EDGE,"E3.1.0"),sQuery(id+"F0.wireOp",EDGE,"E3.2.0"),sQuery(id+"F0.wireOp",EDGE,"E3.3.0"),sQuery(id+"F0.wireOp",EDGE,"E3.4.0"),sQuery(id+"F0.wireOp",EDGE,"E3.5.0"),sQuery(id+"F0.wireOp",EDGE,"E3.6.0"),sQuery(id+"F0.wireOp",EDGE,"E3.7.0"),sQuery(id+"F0.wireOp",EDGE,"E4"),sQuery(id+"F0.wireOp",EDGE,"E5.1.0"),sQuery(id+"F0.wireOp",EDGE,"E5.2.0"),sQuery(id+"F0.wireOp",EDGE,"E5.3.0"),sQuery(id+"F0.wireOp",EDGE,"E5.4.0"),sQuery(id+"F0.wireOp",EDGE,"E5.5.0"),sQuery(id+"F0.wireOp",EDGE,"E5.6.0"),sQuery(id+"F0.wireOp",EDGE,"E5.7.0"),sQuery(id+"F0.wireOp",EDGE,"E6")])],"isStart":false});
            var sketch = newSketch(context, id + "F22", { "sketchPlane" : qUnion([Q0])});
            skCircle(sketch, "E52.0", {"center": v(0, 0) * mm, "radius": 14.38 * mm});
            skCircle(sketch, "E53.0", {"center": v(0, 0) * mm, "radius": 18.38 * mm});
            skSolve(sketch);
        }
        {
            var Q0;
            Q0=makeQuery(id+"F22.imprint","IMPRINT",FACE,{"disambiguationData":[TD([[makeQuery(id+"F22.imprint","IMPRINT",EDGE,{"derivedFrom":sQuery(id+"F22.wireOp",EDGE,"E52.0")}),-1.0]])]});
            extrude(context, id + "F23", {"entities" : qUnion([Q0]), "operationType" : NewBodyOperationType.ADD, "depth" : 4 * mm, "offsetDistance" : 25 * mm});
        }
        {
            var Q0;
            Q0=makeQuery(id+"F23.opExtrude","CAP_EDGE",EDGE,{"disambiguationData":[OSD([sQuery(id+"F22.wireOp",EDGE,"E53.0")])],"isStart":false});
            chamfer(context, id + "F24", {"entities" : qUnion([Q0]), "width" : 2.9 * mm, "tangentPropagation" : true});
        }
        {
            var Q0;
            Q0=makeQuery(id+"F23.opExtrude","CAP_EDGE",EDGE,{"disambiguationData":[OSD([sQuery(id+"F22.wireOp",EDGE,"E53.0")])],"isStart":true});
            var Q1;
            {var subQ0=sQuery(id+"F22.wireOp",EDGE,"E53.0");Q1=makeQuery(id+"F24.opChamfer","BLEND_EDGE",EDGE,{"blendedFrom":[makeQuery(id+"F23.opExtrude","CAP_EDGE",EDGE,{"disambiguationData":[OSD([subQ0])],"isStart":false}),makeQuery(id+"F23.opExtrude","CAP_FACE",FACE,{"disambiguationData":[OSD([sQuery(id+"F22.wireOp",EDGE,"E52.0"),subQ0])],"isStart":false})],"blendedInto":[makeQuery(id+"F23.opExtrude","CAP_FACE",FACE,{"disambiguationData":[OSD([sQuery(id+"F22.wireOp",EDGE,"E52.0"),subQ0])],"isStart":false})]});}
            var Q2;
            {var subQ0=sQuery(id+"F22.wireOp",EDGE,"E53.0");Q2=makeQuery(id+"F24.opChamfer","BLEND_EDGE",EDGE,{"blendedFrom":[makeQuery(id+"F23.opExtrude","CAP_EDGE",EDGE,{"disambiguationData":[OSD([subQ0])],"isStart":false}),makeQuery(id+"F23.opExtrude","SWEPT_FACE",FACE,{"disambiguationData":[OSD([subQ0])]})],"blendedInto":[makeQuery(id+"F23.opExtrude","SWEPT_FACE",FACE,{"disambiguationData":[OSD([subQ0])]})]});}
            fillet(context, id + "F25", {"entities" : qUnion([Q0, Q1, Q2]), "radius" : .75 * mm, "tangentPropagation" : true, "allowEdgeOverflow" : false});
        }
    });
